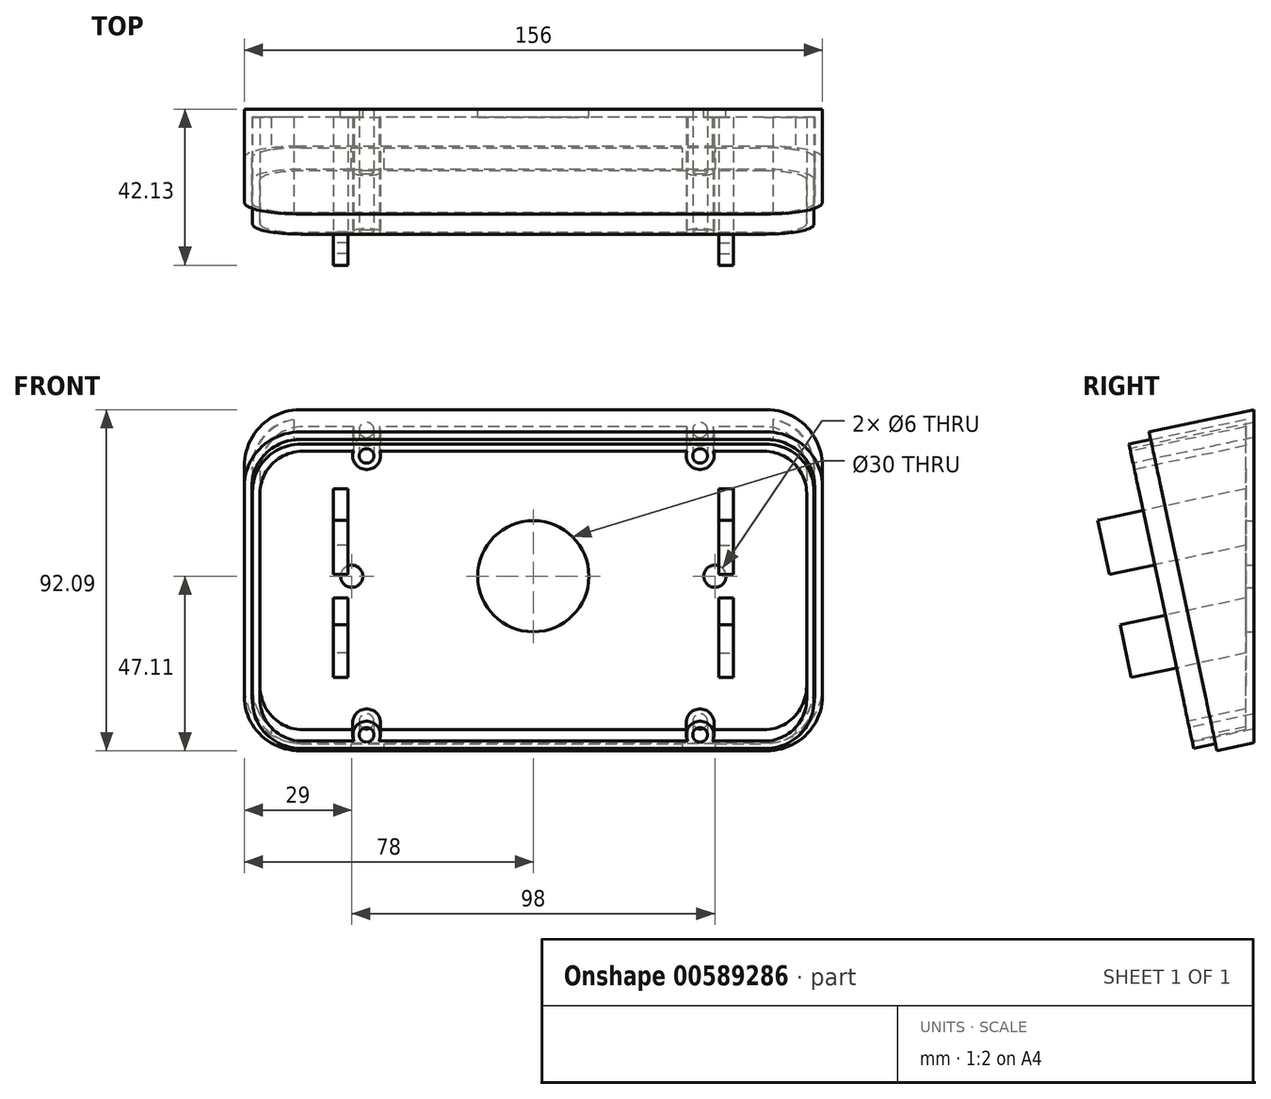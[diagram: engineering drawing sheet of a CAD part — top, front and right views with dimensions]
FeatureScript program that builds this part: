
annotation { "Feature Type Name" : "Feature", "Feature Type Description" : "" }
export const myFeature = defineFeature(function(context is Context, id is Id, definition is map)
    precondition{}
    {
        {
            var Q0;
            Q0=qCreatedBy(makeId("Front.planeOp"),FACE);
            cPlane(context, id + "F0", {"entities" : qUnion([Q0]), "cplaneType" : CPlaneType.OFFSET, "offset" : 20 * mm, "width" : 150 * mm, "height" : 150 * mm});
        }
        {
            var Q0;
            Q0=qCreatedBy(id+"F0.planeOp",FACE);
            var sketch = newSketch(context, id + "F1", { "sketchPlane" : qUnion([Q0])});
            skLineSegment(sketch, "E0", {"start": v(-67.43, 0) * mm, "end": v(64.52, 0) * mm});
            skSolve(sketch);
        }
        {
            var Q0;
            Q0=qCreatedBy(makeId("Front.planeOp"),FACE);
            var Q1;
            Q1=sQuery(id+"F1.wireOp",EDGE,"E0");
            cPlane(context, id + "F2", {"entities" : qUnion([Q0, Q1]), "cplaneType" : CPlaneType.LINE_ANGLE, "offset" : 15 * mm, "angle" : 12 * degree, "width" : 150 * mm, "height" : 150 * mm});
        }
        {
            var Q0;
            Q0=qCreatedBy(id+"F2.planeOp",FACE);
            var sketch = newSketch(context, id + "F3", { "sketchPlane" : qUnion([Q0])});
            skLineSegment(sketch, "E1.bottom", {"start": v(-63, 44) * mm, "end": v(63, 44) * mm});
            skLineSegment(sketch, "E1.top", {"start": v(-63, -44) * mm, "end": v(63, -44) * mm});
            skLineSegment(sketch, "E1.left", {"start": v(-78, 29) * mm, "end": v(-78, -29) * mm});
            skLineSegment(sketch, "E1.right", {"start": v(78, 29) * mm, "end": v(78, -29) * mm});
            skPoint(sketch, "E1.middle", {"position": v(0, 0) * mm});
            skPoint(sketch, "E2.visualSharp", {"position": v(-78, 44) * mm});
            skArc(sketch, "E2.filletArc", {"start": v(-63, 44) * mm, "mid": v(-73.6, 39.6) * mm, "end": v(-78, 29) * mm});
            skPoint(sketch, "E3.visualSharp", {"position": v(78, 44) * mm});
            skArc(sketch, "E3.filletArc", {"start": v(78, 29) * mm, "mid": v(73.6, 39.6) * mm, "end": v(63, 44) * mm});
            skPoint(sketch, "E4.visualSharp", {"position": v(78, -44) * mm});
            skArc(sketch, "E4.filletArc", {"start": v(63, -44) * mm, "mid": v(73.6, -39.6) * mm, "end": v(78, -29) * mm});
            skPoint(sketch, "E5.visualSharp", {"position": v(-78, -44) * mm});
            skArc(sketch, "E5.filletArc", {"start": v(-78, -29) * mm, "mid": v(-73.6, -39.6) * mm, "end": v(-63, -44) * mm});
            skSolve(sketch);
        }
        {
            var Q0;
            Q0=qSketchRegion(id+"F3",true);
            var Q1;
            Q1=qCreatedBy(makeId("Front.planeOp"),FACE);
            extrude(context, id + "F4", {"entities" : qUnion([Q0]), "endBound" : BoundingType.UP_TO_SURFACE, "endBoundEntityFace" : qUnion([Q1]), "depth" : 20 * mm, "offsetDistance" : 25 * mm});
        }
        {
            var Q0;
            Q0=makeQuery(id+"F4.opExtrude","CAP_FACE",FACE,{"disambiguationData":[OSD([sQuery(id+"F3.wireOp",EDGE,"E1.bottom"),sQuery(id+"F3.wireOp",EDGE,"E1.top"),sQuery(id+"F3.wireOp",EDGE,"E1.left"),sQuery(id+"F3.wireOp",EDGE,"E1.right"),sQuery(id+"F3.wireOp",EDGE,"E2.filletArc"),sQuery(id+"F3.wireOp",EDGE,"E3.filletArc"),sQuery(id+"F3.wireOp",EDGE,"E4.filletArc"),sQuery(id+"F3.wireOp",EDGE,"E5.filletArc")])],"isStart":true});
            shell(context, id + "F5", {"entities" : qUnion([Q0]), "thickness" : 2.1 * mm});
        }
        {
            var Q0;
            Q0=qCreatedBy(makeId("Front.planeOp"),FACE);
            var sketch = newSketch(context, id + "F6", { "sketchPlane" : qUnion([Q0])});
            skCircle(sketch, "E6", {"center": v(0, 0) * mm, "radius": 15 * mm});
            skCircle(sketch, "E7", {"center": v(-49, 0) * mm, "radius": 3 * mm});
            skCircle(sketch, "E8.MirrorC", {"center": v(49, 0) * mm, "radius": 3 * mm});
            skSolve(sketch);
        }
        {
            var Q0;
            Q0=qSketchRegion(id+"F6",true);
            extrude(context, id + "F7", {"entities" : qUnion([Q0]), "operationType" : NewBodyOperationType.REMOVE, "depth" : 25 * mm, "offsetDistance" : 25 * mm});
        }
        {
            var Q0;
            Q0=qCreatedBy(id+"F2.planeOp",FACE);
            cPlane(context, id + "F8", {"entities" : qUnion([Q0]), "cplaneType" : CPlaneType.OFFSET, "offset" : 6 * mm, "oppositeDirection" : true, "width" : 150 * mm, "height" : 150 * mm});
        }
        {
            var Q0;
            Q0=qCreatedBy(id+"F8.planeOp",FACE);
            var sketch = newSketch(context, id + "F9", { "sketchPlane" : qUnion([Q0])});
            skLineSegment(sketch, "E9.bottom", {"start": v(-62.75, 41.93) * mm, "end": v(62.75, 41.93) * mm});
            skLineSegment(sketch, "E9.top", {"start": v(-62.75, -42.07) * mm, "end": v(62.75, -42.07) * mm});
            skLineSegment(sketch, "E9.left", {"start": v(-75.75, 28.93) * mm, "end": v(-75.75, -29.07) * mm});
            skLineSegment(sketch, "E9.right", {"start": v(75.75, 28.93) * mm, "end": v(75.75, -29.07) * mm});
            skPoint(sketch, "E9.middle", {"position": v(0, -0.07) * mm});
            skPoint(sketch, "E10.visualSharp", {"position": v(-75.75, 41.93) * mm});
            skArc(sketch, "E10.filletArc", {"start": v(-62.75, 41.93) * mm, "mid": v(-71.94, 38.13) * mm, "end": v(-75.75, 28.93) * mm});
            skPoint(sketch, "E11.visualSharp", {"position": v(75.75, 41.93) * mm});
            skArc(sketch, "E11.filletArc", {"start": v(75.75, 28.93) * mm, "mid": v(71.94, 38.13) * mm, "end": v(62.75, 41.93) * mm});
            skPoint(sketch, "E12.visualSharp", {"position": v(75.75, -42.07) * mm});
            skArc(sketch, "E12.filletArc", {"start": v(62.75, -42.07) * mm, "mid": v(71.94, -38.26) * mm, "end": v(75.75, -29.07) * mm});
            skPoint(sketch, "E13.visualSharp", {"position": v(-75.75, -42.07) * mm});
            skArc(sketch, "E13.filletArc", {"start": v(-75.75, -29.07) * mm, "mid": v(-71.94, -38.26) * mm, "end": v(-62.75, -42.07) * mm});
            skLineSegment(sketch, "E14.bottom", {"start": v(-62.25, 39.93) * mm, "end": v(62.25, 39.93) * mm});
            skLineSegment(sketch, "E14.top", {"start": v(-62.25, -40.07) * mm, "end": v(62.25, -40.07) * mm});
            skLineSegment(sketch, "E14.left", {"start": v(-73.75, 28.43) * mm, "end": v(-73.75, -28.57) * mm});
            skLineSegment(sketch, "E14.right", {"start": v(73.75, 28.43) * mm, "end": v(73.75, -28.57) * mm});
            skPoint(sketch, "E15.visualSharp", {"position": v(-73.75, 39.93) * mm});
            skArc(sketch, "E15.filletArc", {"start": v(-62.25, 39.93) * mm, "mid": v(-70.38, 36.57) * mm, "end": v(-73.75, 28.43) * mm});
            skPoint(sketch, "E16.visualSharp", {"position": v(73.75, 39.93) * mm});
            skArc(sketch, "E16.filletArc", {"start": v(73.75, 28.43) * mm, "mid": v(70.38, 36.57) * mm, "end": v(62.25, 39.93) * mm});
            skPoint(sketch, "E17.visualSharp", {"position": v(73.75, -40.07) * mm});
            skArc(sketch, "E17.filletArc", {"start": v(62.25, -40.07) * mm, "mid": v(70.38, -36.7) * mm, "end": v(73.75, -28.57) * mm});
            skPoint(sketch, "E18.visualSharp", {"position": v(-73.75, -40.07) * mm});
            skArc(sketch, "E18.filletArc", {"start": v(-73.75, -28.57) * mm, "mid": v(-70.38, -36.7) * mm, "end": v(-62.25, -40.07) * mm});
            skSolve(sketch);
        }
        {
            var Q0;
            Q0=qSketchRegion(id+"F9",true);
            var Q1;
            Q1=qCreatedBy(makeId("Front.planeOp"),FACE);
            extrude(context, id + "F10", {"entities" : qUnion([Q0]), "operationType" : NewBodyOperationType.ADD, "endBound" : BoundingType.UP_TO_SURFACE, "depth" : 25 * mm, "endBoundEntityFace" : qUnion([Q1]), "offsetDistance" : 25 * mm});
        }
        {
            var Q0;
            Q0=qCreatedBy(id+"F2.planeOp",FACE);
            cPlane(context, id + "F11", {"entities" : qUnion([Q0]), "cplaneType" : CPlaneType.OFFSET, "offset" : 18.5 * mm, "oppositeDirection" : true, "width" : 150 * mm, "height" : 150 * mm});
        }
        {
            var Q0;
            Q0=qCreatedBy(makeId("Front.planeOp"),FACE);
            cPlane(context, id + "F12", {"entities" : qUnion([Q0]), "cplaneType" : CPlaneType.OFFSET, "offset" : 2.5 * mm, "width" : 150 * mm, "height" : 150 * mm});
        }
        {
            var Q0;
            Q0=sQuery(id+"F1.wireOp",EDGE,"E0");
            cPlane(context, id + "F13", {"entities" : qUnion([Q0]), "cplaneType" : CPlaneType.LINE_ANGLE, "offset" : 25 * mm, "angle" : 81 * degree, "oppositeDirection" : true, "width" : 150 * mm, "height" : 150 * mm});
        }
        {
            var Q0;
            Q0=qCreatedBy(id+"F11.planeOp",FACE);
            var sketch = newSketch(context, id + "F14", { "sketchPlane" : qUnion([Q0])});
            skLineSegment(sketch, "E19.bottom", {"start": v(50, -5.3) * mm, "end": v(54, -5.3) * mm});
            skLineSegment(sketch, "E19.top", {"start": v(50, -19.87) * mm, "end": v(54, -19.87) * mm});
            skLineSegment(sketch, "E19.left", {"start": v(50, -5.3) * mm, "end": v(50, -19.87) * mm});
            skLineSegment(sketch, "E19.right", {"start": v(54, -5.3) * mm, "end": v(54, -19.87) * mm});
            skPoint(sketch, "E19.middle", {"position": v(52, -12.59) * mm});
            skLineSegment(sketch, "E20.bottom", {"start": v(50, 23.57) * mm, "end": v(54, 23.57) * mm});
            skLineSegment(sketch, "E20.top", {"start": v(50, 8.57) * mm, "end": v(54, 8.57) * mm});
            skLineSegment(sketch, "E20.left", {"start": v(50, 23.57) * mm, "end": v(50, 8.57) * mm});
            skLineSegment(sketch, "E20.right", {"start": v(54, 23.57) * mm, "end": v(54, 8.57) * mm});
            skLineSegment(sketch, "E21", {"start": v(0, 29.74) * mm, "end": v(0, -30.95) * mm});
            skLineSegment(sketch, "E22.MirrorCS", {"start": v(-50, 23.57) * mm, "end": v(-54, 23.57) * mm});
            skLineSegment(sketch, "E23.MirrorCS", {"start": v(-54, 23.57) * mm, "end": v(-54, 8.57) * mm});
            skLineSegment(sketch, "E24.MirrorCS", {"start": v(-50, 23.57) * mm, "end": v(-50, 8.57) * mm});
            skLineSegment(sketch, "E25.MirrorCS", {"start": v(-50, 8.57) * mm, "end": v(-54, 8.57) * mm});
            skLineSegment(sketch, "E26.MirrorCS", {"start": v(-50, -5.3) * mm, "end": v(-54, -5.3) * mm});
            skLineSegment(sketch, "E27.MirrorCS", {"start": v(-50, -5.3) * mm, "end": v(-50, -19.87) * mm});
            skLineSegment(sketch, "E28.MirrorCS", {"start": v(-54, -5.3) * mm, "end": v(-54, -19.87) * mm});
            skLineSegment(sketch, "E29.MirrorCS", {"start": v(-50, -19.87) * mm, "end": v(-54, -19.87) * mm});
            skSolve(sketch);
        }
        {
            var Q0;
            Q0=qSketchRegion(id+"F14",true);
            var Q1;
            Q1=qCreatedBy(makeId("Front.planeOp"),FACE);
            extrude(context, id + "F15", {"entities" : qUnion([Q0]), "operationType" : NewBodyOperationType.ADD, "endBound" : BoundingType.UP_TO_SURFACE, "depth" : 25 * mm, "endBoundEntityFace" : qUnion([Q1]), "offsetDistance" : 25 * mm});
        }
        {
            var Q0;
            Q0=qCreatedBy(id+"F8.planeOp",FACE);
            var sketch = newSketch(context, id + "F16", { "sketchPlane" : qUnion([Q0])});
            skCircle(sketch, "E30", {"center": v(45, 38.66) * mm, "radius": 3.75 * mm});
            skCircle(sketch, "E31.MirrorC", {"center": v(-45, 38.66) * mm, "radius": 3.75 * mm});
            skCircle(sketch, "E32", {"center": v(45, -38.34) * mm, "radius": 3.75 * mm});
            skCircle(sketch, "E33.MirrorC", {"center": v(-45, -38.34) * mm, "radius": 3.75 * mm});
            skSolve(sketch);
        }
        {
            var Q0;
            Q0 = qSketchRegion(id + "F16", true);
            var Q1;
            Q1=qCreatedBy(makeId("Front.planeOp"),FACE);
            extrude(context, id + "F17", {"entities" : qUnion([Q0]), "operationType" : NewBodyOperationType.ADD, "endBound" : BoundingType.UP_TO_SURFACE, "depth" : 25 * mm, "endBoundEntityFace" : qUnion([Q1]), "offsetDistance" : 25 * mm});
        }
        {
            var Q0;
            Q0=qCreatedBy(id+"F8.planeOp",FACE);
            var sketch = newSketch(context, id + "F18", { "sketchPlane" : qUnion([Q0])});
            skCircle(sketch, "E34", {"center": v(45, 38.66) * mm, "radius": 2 * mm});
            skCircle(sketch, "E35.MirrorC", {"center": v(-45, 38.66) * mm, "radius": 2 * mm});
            skCircle(sketch, "E36", {"center": v(45, -38.34) * mm, "radius": 2 * mm});
            skCircle(sketch, "E37.MirrorC", {"center": v(-45, -38.34) * mm, "radius": 2 * mm});
            skSolve(sketch);
        }
        {
            var Q0;
            Q0 = qSketchRegion(id + "F18", true);
            var Q1;
            Q1=qCreatedBy(makeId("Front.planeOp"),FACE);
            extrude(context, id + "F19", {"entities" : qUnion([Q0]), "operationType" : NewBodyOperationType.REMOVE, "endBound" : BoundingType.UP_TO_SURFACE, "depth" : 25 * mm, "endBoundEntityFace" : qUnion([Q1]), "offsetDistance" : 25 * mm});
        }
        {
            var Q0;
            Q0=qCreatedBy(id+"F2.planeOp",FACE);
            var sketch = newSketch(context, id + "F20", { "sketchPlane" : qUnion([Q0])});
            skLineSegment(sketch, "E38.bottom", {"start": v(50.53, 50.46) * mm, "end": v(39.2, 50.46) * mm});
            skLineSegment(sketch, "E38.top", {"start": v(50.53, 41.93) * mm, "end": v(39.2, 41.93) * mm});
            skLineSegment(sketch, "E38.left", {"start": v(50.53, 50.46) * mm, "end": v(50.53, 41.93) * mm});
            skLineSegment(sketch, "E38.right", {"start": v(39.2, 50.46) * mm, "end": v(39.2, 41.93) * mm});
            skLineSegment(sketch, "E39.MirrorCS", {"start": v(-50.53, 50.46) * mm, "end": v(-39.2, 50.46) * mm});
            skLineSegment(sketch, "E40.MirrorCS", {"start": v(-50.53, 50.46) * mm, "end": v(-50.53, 41.93) * mm});
            skLineSegment(sketch, "E41.MirrorCS", {"start": v(-50.53, 41.93) * mm, "end": v(-39.2, 41.93) * mm});
            skLineSegment(sketch, "E42.MirrorCS", {"start": v(-39.2, 50.46) * mm, "end": v(-39.2, 41.93) * mm});
            skLineSegment(sketch, "E43.bottom", {"start": v(49.16, -42.05) * mm, "end": v(40.3, -42.05) * mm});
            skLineSegment(sketch, "E43.top", {"start": v(49.16, -44.98) * mm, "end": v(40.3, -44.98) * mm});
            skLineSegment(sketch, "E43.left", {"start": v(49.16, -42.05) * mm, "end": v(49.16, -44.98) * mm});
            skLineSegment(sketch, "E43.right", {"start": v(40.3, -42.05) * mm, "end": v(40.3, -44.98) * mm});
            skLineSegment(sketch, "E44.MirrorCS", {"start": v(-40.3, -42.05) * mm, "end": v(-40.3, -44.98) * mm});
            skLineSegment(sketch, "E45.MirrorCS", {"start": v(-49.16, -42.05) * mm, "end": v(-40.3, -42.05) * mm});
            skLineSegment(sketch, "E46.MirrorCS", {"start": v(-49.16, -42.05) * mm, "end": v(-49.16, -44.98) * mm});
            skLineSegment(sketch, "E47.MirrorCS", {"start": v(-49.16, -44.98) * mm, "end": v(-40.3, -44.98) * mm});
            skSolve(sketch);
        }
        {
            var Q0;
            Q0 = qSketchRegion(id + "F20", true);
            extrude(context, id + "F21", {"entities" : qUnion([Q0]), "operationType" : NewBodyOperationType.REMOVE, "oppositeDirection" : true, "depth" : 25 * mm, "offsetDistance" : 25 * mm});
        }
    });
